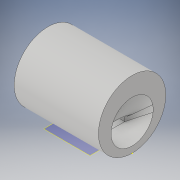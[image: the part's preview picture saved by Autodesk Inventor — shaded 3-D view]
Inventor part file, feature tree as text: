
AUTODESK INVENTOR PART (.ipt)
format: ipt  version: 2019 (Build 230136000, 136)  size: 235,520 bytes
history: native  units: in
note: dims shown in document units (in); Inventor stores cm internally (conversion verified against a paired STEP export)
features: sketch x7, extrude x2, revolve x1, loft x1, fillet x1, plane x1, other x1
ambient origin geometry x8: Origin, YZ Plane, XZ Plane, XY Plane, X Axis, Y Axis, Z Axis, Center Point
bodies: Solid1 (feature_tree)
feature tree (14):
  revolve  "Revolution1"  [1 undecoded]
  sketch  "Sketch2"  dims[d3=0.7874in d4=90.0deg]
  extrude  "Extrusion1"  TaperAngle=90.0deg  [1 undecoded]
  sketch  "Sketch4"  dims[d9=0.7874in d10=0.0in d11=90.0deg]
  sketch  "Sketch5"  dims[d12=0.0in d13=90.0deg]
  loft  "Loft1"
  fillet  "Fillet1"  Radius=0.3937in
  sketch  "Sketch6"  dims[d14=0.2362in]
  plane  "Work Plane1"
  extrude  "Extrusion2"  TaperAngle=0.0deg  [1 undecoded]
  sketch  "Sketch1"  dims[d0=0.1181in d1=0.7874in]
  sketch  "Sketch3"  dims[d5=0.0591in d6=0.5118in d7=0.3937in d8=0.0in]
  other  "Edges1"
  sketch  "Sketch7"  dims[d15=0.5118in d16=0.1969in d17=0.0in d18=0.6299in d19=0.7177in]
note: 3 required parameter values undecoded (feature->parameter linkage not recoverable at this tier; creation-order binding heuristic only, values carry confidence <= 0.55)